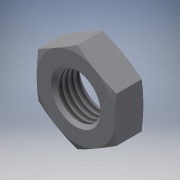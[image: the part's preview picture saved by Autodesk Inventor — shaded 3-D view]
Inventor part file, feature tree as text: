
AUTODESK INVENTOR PART (.ipt)
format: ipt  version: 2018 (Build 220112000, 112)  size: 174,592 bytes
history: native  units: in
note: dims shown in document units (in); Inventor stores cm internally (conversion verified against a paired STEP export)
features: other x70, sketch x3, revolve x2, extrude x1, thread x1
ambient origin geometry x8: Origin, YZ Plane, XZ Plane, XY Plane, X Axis, Y Axis, Z Axis, Center Point
bodies: Solid1 (feature_tree)
feature tree (77):
  sketch  "Sketch_8"  dims[d0=360.0deg d1=0.25in d2=0.0in]
  sketch  "Sketch_10"  dims[d3=360.0deg d4=0.1959in d5=0.0in]
  revolve  "Revolution1"  [1 undecoded]
  extrude  "Extrusion1"  Depth=0.1959in TaperAngle=0.0deg
  revolve  "Revolution2"  [1 undecoded]
  thread  "Thread1"  [1 undecoded]
  other  "NUT_XY"
  other  "NUT_YZ"
  other  "NUT_ZX"
  other  "NUT_X"
  other  "NUT_Y"
  other  "NUT_Z"
  other  "NUT_Center"
  other  "a1_XY"
  other  "a1_YZ"
  other  "a1_ZX"
  other  "a1_X"
  other  "a1_Y"
  other  "a1_Z"
  other  "a1_Center"
  other  "a2_XY"
  other  "a2_YZ"
  other  "a2_ZX"
  other  "a2_X"
  other  "a2_Y"
  other  "a2_Z"
  other  "a2_Center"
  other  "b1_XY"
  other  "b1_YZ"
  other  "b1_ZX"
  other  "b1_X"
  other  "b1_Y"
  other  "b1_Z"
  other  "b1_Center"
  other  "b2_XY"
  other  "b2_YZ"
  other  "b2_ZX"
  other  "b2_X"
  other  "b2_Y"
  other  "b2_Z"
  other  "b2_Center"
  other  "e_XY"
  other  "e_YZ"
  other  "e_ZX"
  other  "e_X"
  other  "e_Y"
  other  "e_Z"
  other  "e_Center"
  other  "ol1_XY"
  other  "ol1_YZ"
  other  "ol1_ZX"
  other  "ol1_X"
  other  "ol1_Y"
  other  "ol1_Z"
  other  "ol1_Center"
  other  "ol2_XY"
  other  "ol2_YZ"
  other  "ol2_ZX"
  other  "ol2_X"
  other  "ol2_Y"
  other  "ol2_Z"
  other  "ol2_Center"
  other  "th1_XY"
  other  "th1_YZ"
  other  "th1_ZX"
  other  "th1_X"
  other  "th1_Y"
  other  "th1_Z"
  other  "th1_Center"
  other  "th2_XY"
  other  "th2_YZ"
  other  "th2_ZX"
  other  "th2_X"
  other  "th2_Y"
  other  "th2_Z"
  other  "th2_Center"
  sketch  "Sketch_11"  dims[d6=0.0in d7=0.0in d8=0.0in]
note: 3 required parameter values undecoded (feature->parameter linkage not recoverable at this tier; creation-order binding heuristic only, values carry confidence <= 0.55)